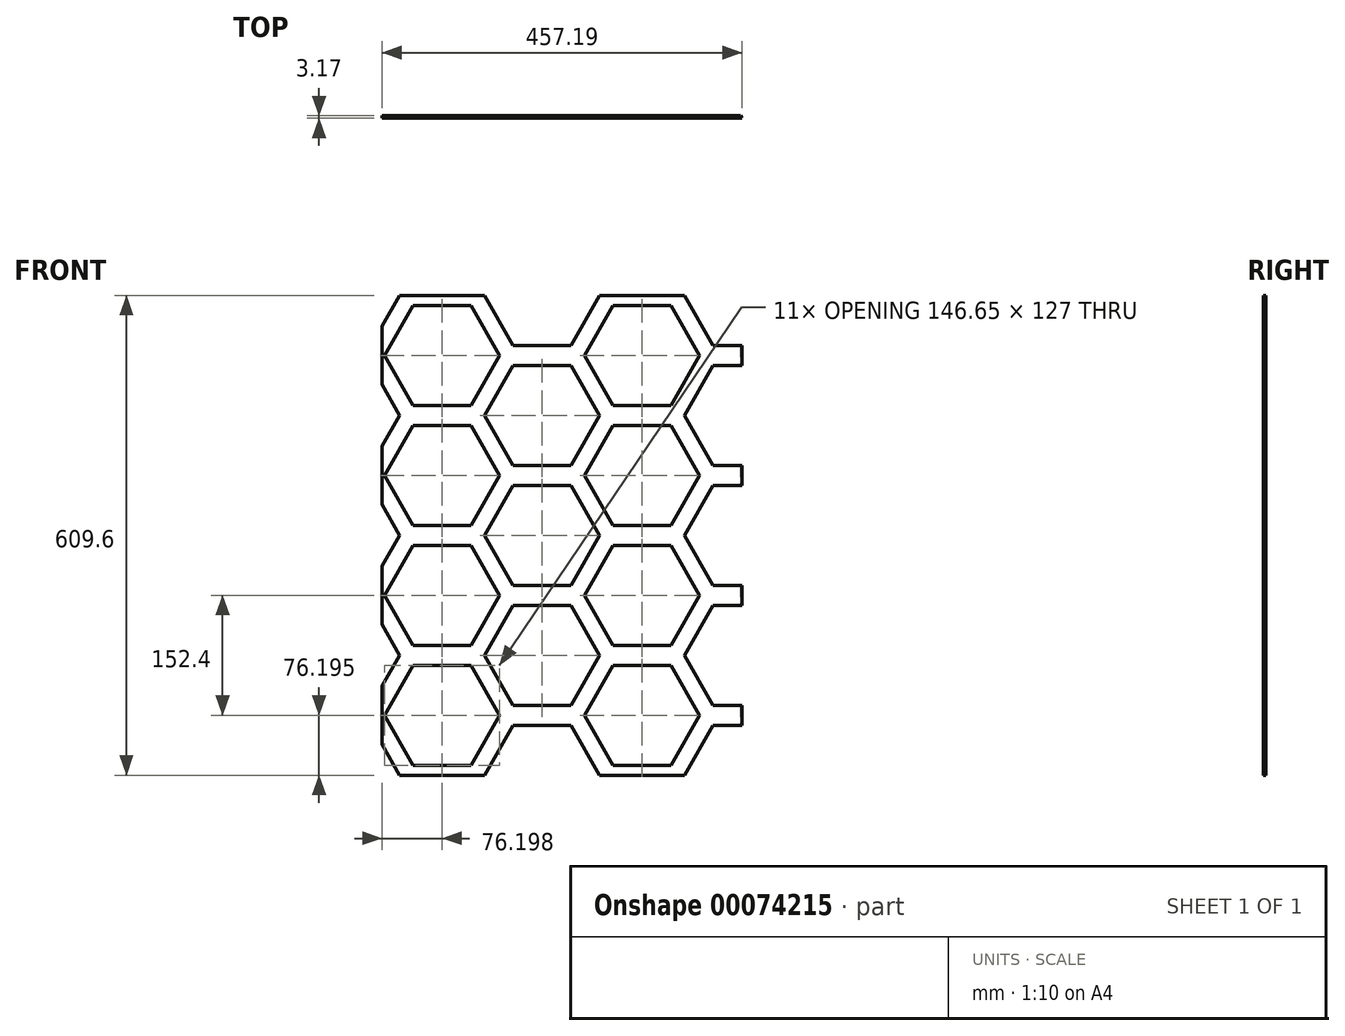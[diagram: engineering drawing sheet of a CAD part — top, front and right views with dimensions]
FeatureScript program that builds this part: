
annotation { "Feature Type Name" : "Feature", "Feature Type Description" : "" }
export const myFeature = defineFeature(function(context is Context, id is Id, definition is map)
    precondition{}
    {
        {
            var Q0;
            Q0=qCreatedBy(makeId("Front.planeOp"),FACE);
            var sketch = newSketch(context, id + "F0", { "sketchPlane" : qUnion([Q0])});
            skLineSegment(sketch, "E0.bottom", {"start": v(-264.83, 118.46) * mm, "end": v(192.37, 118.46) * mm});
            skLineSegment(sketch, "E0.top", {"start": v(-264.83, -491.14) * mm, "end": v(192.37, -491.14) * mm});
            skLineSegment(sketch, "E0.left", {"start": v(-264.83, 118.46) * mm, "end": v(-264.83, -491.14) * mm});
            skLineSegment(sketch, "E0.right", {"start": v(192.37, 118.46) * mm, "end": v(192.37, -491.14) * mm});
            skLineSegment(sketch, "E1", {"start": v(-188.63, -491.14) * mm, "end": v(-188.63, 518.04) * mm, "construction": true});
            skLineSegment(sketch, "E2", {"start": v(-264.83, -414.94) * mm, "end": v(579.47, -414.94) * mm, "construction": true});
            skCircle(sketch, "E3.cCircle", {"center": v(-188.63, -414.94) * mm, "radius": 63.5 * mm, "construction": true});
            skLineSegment(sketch, "E3.0", {"start": v(-225.3, -351.44) * mm, "end": v(-151.97, -351.44) * mm});
            skLineSegment(sketch, "E3.1", {"start": v(-151.97, -351.44) * mm, "end": v(-115.3, -414.94) * mm});
            skLineSegment(sketch, "E3.2", {"start": v(-115.3, -414.94) * mm, "end": v(-151.97, -478.44) * mm});
            skLineSegment(sketch, "E3.3", {"start": v(-151.97, -478.44) * mm, "end": v(-225.3, -478.44) * mm});
            skLineSegment(sketch, "E3.4", {"start": v(-225.3, -478.44) * mm, "end": v(-261.96, -414.94) * mm});
            skLineSegment(sketch, "E3.5", {"start": v(-261.96, -414.94) * mm, "end": v(-225.3, -351.44) * mm});
            skPoint(sketch, "E3.0.midPoint", {"position": v(-188.63, -351.44) * mm});
            skLineSegment(sketch, "E4", {"start": v(-188.63, -414.94) * mm, "end": v(-315.63, -414.94) * mm, "construction": true});
            skLineSegment(sketch, "E5", {"start": v(-315.63, -414.94) * mm, "end": v(-315.63, -491.14) * mm, "construction": true});
            skCircle(sketch, "E6.cCircle", {"center": v(-315.63, -491.14) * mm, "radius": 63.5 * mm, "construction": true});
            skLineSegment(sketch, "E6.0", {"start": v(-352.3, -427.64) * mm, "end": v(-278.97, -427.64) * mm});
            skLineSegment(sketch, "E6.1", {"start": v(-278.97, -427.64) * mm, "end": v(-242.3, -491.14) * mm});
            skLineSegment(sketch, "E6.2", {"start": v(-242.3, -491.14) * mm, "end": v(-278.97, -554.64) * mm});
            skLineSegment(sketch, "E6.3", {"start": v(-278.97, -554.64) * mm, "end": v(-352.3, -554.64) * mm});
            skLineSegment(sketch, "E6.4", {"start": v(-352.3, -554.64) * mm, "end": v(-388.96, -491.14) * mm});
            skLineSegment(sketch, "E6.5", {"start": v(-388.96, -491.14) * mm, "end": v(-352.3, -427.64) * mm});
            skPoint(sketch, "E6.0.midPoint", {"position": v(-315.63, -427.64) * mm});
            skLineSegment(sketch, "E7.0.1.0", {"start": v(-151.97, -326.04) * mm, "end": v(-225.3, -326.04) * mm});
            skLineSegment(sketch, "E7.0.1.1", {"start": v(-225.3, -199.04) * mm, "end": v(-151.97, -199.04) * mm});
            skLineSegment(sketch, "E7.0.1.2", {"start": v(-225.3, -326.04) * mm, "end": v(-261.96, -262.54) * mm});
            skLineSegment(sketch, "E7.0.1.3", {"start": v(-151.97, -199.04) * mm, "end": v(-115.3, -262.54) * mm});
            skLineSegment(sketch, "E7.0.1.4", {"start": v(-261.96, -262.54) * mm, "end": v(-225.3, -199.04) * mm});
            skLineSegment(sketch, "E7.0.1.5", {"start": v(-115.3, -262.54) * mm, "end": v(-151.97, -326.04) * mm});
            skLineSegment(sketch, "E7.0.2.0", {"start": v(-151.97, -173.64) * mm, "end": v(-225.3, -173.64) * mm});
            skLineSegment(sketch, "E7.0.2.1", {"start": v(-225.3, -46.64) * mm, "end": v(-151.97, -46.64) * mm});
            skLineSegment(sketch, "E7.0.2.2", {"start": v(-225.3, -173.64) * mm, "end": v(-261.96, -110.14) * mm});
            skLineSegment(sketch, "E7.0.2.3", {"start": v(-151.97, -46.64) * mm, "end": v(-115.3, -110.14) * mm});
            skLineSegment(sketch, "E7.0.2.4", {"start": v(-261.96, -110.14) * mm, "end": v(-225.3, -46.64) * mm});
            skLineSegment(sketch, "E7.0.2.5", {"start": v(-115.3, -110.14) * mm, "end": v(-151.97, -173.64) * mm});
            skLineSegment(sketch, "E7.0.3.0", {"start": v(-151.97, -21.24) * mm, "end": v(-225.3, -21.24) * mm});
            skLineSegment(sketch, "E7.0.3.1", {"start": v(-225.3, 105.76) * mm, "end": v(-151.97, 105.76) * mm});
            skLineSegment(sketch, "E7.0.3.2", {"start": v(-225.3, -21.24) * mm, "end": v(-261.96, 42.26) * mm});
            skLineSegment(sketch, "E7.0.3.3", {"start": v(-151.97, 105.76) * mm, "end": v(-115.3, 42.26) * mm});
            skLineSegment(sketch, "E7.0.3.4", {"start": v(-261.96, 42.26) * mm, "end": v(-225.3, 105.76) * mm});
            skLineSegment(sketch, "E7.0.3.5", {"start": v(-115.3, 42.26) * mm, "end": v(-151.97, -21.24) * mm});
            skLineSegment(sketch, "E7.1.0.0", {"start": v(102.03, -478.44) * mm, "end": v(28.7, -478.44) * mm});
            skLineSegment(sketch, "E7.1.0.1", {"start": v(28.7, -351.44) * mm, "end": v(102.03, -351.44) * mm});
            skLineSegment(sketch, "E7.1.0.2", {"start": v(28.7, -478.44) * mm, "end": v(-7.96, -414.94) * mm});
            skLineSegment(sketch, "E7.1.0.3", {"start": v(102.03, -351.44) * mm, "end": v(138.7, -414.94) * mm});
            skLineSegment(sketch, "E7.1.0.4", {"start": v(-7.96, -414.94) * mm, "end": v(28.7, -351.44) * mm});
            skLineSegment(sketch, "E7.1.0.5", {"start": v(138.7, -414.94) * mm, "end": v(102.03, -478.44) * mm});
            skLineSegment(sketch, "E7.1.1.0", {"start": v(102.03, -326.04) * mm, "end": v(28.7, -326.04) * mm});
            skLineSegment(sketch, "E7.1.1.1", {"start": v(28.7, -199.04) * mm, "end": v(102.03, -199.04) * mm});
            skLineSegment(sketch, "E7.1.1.2", {"start": v(28.7, -326.04) * mm, "end": v(-7.96, -262.54) * mm});
            skLineSegment(sketch, "E7.1.1.3", {"start": v(102.03, -199.04) * mm, "end": v(138.7, -262.54) * mm});
            skLineSegment(sketch, "E7.1.1.4", {"start": v(-7.96, -262.54) * mm, "end": v(28.7, -199.04) * mm});
            skLineSegment(sketch, "E7.1.1.5", {"start": v(138.7, -262.54) * mm, "end": v(102.03, -326.04) * mm});
            skLineSegment(sketch, "E7.1.2.0", {"start": v(102.03, -173.64) * mm, "end": v(28.7, -173.64) * mm});
            skLineSegment(sketch, "E7.1.2.1", {"start": v(28.7, -46.64) * mm, "end": v(102.03, -46.64) * mm});
            skLineSegment(sketch, "E7.1.2.2", {"start": v(28.7, -173.64) * mm, "end": v(-7.96, -110.14) * mm});
            skLineSegment(sketch, "E7.1.2.3", {"start": v(102.03, -46.64) * mm, "end": v(138.7, -110.14) * mm});
            skLineSegment(sketch, "E7.1.2.4", {"start": v(-7.96, -110.14) * mm, "end": v(28.7, -46.64) * mm});
            skLineSegment(sketch, "E7.1.2.5", {"start": v(138.7, -110.14) * mm, "end": v(102.03, -173.64) * mm});
            skLineSegment(sketch, "E7.1.3.0", {"start": v(102.03, -21.24) * mm, "end": v(28.7, -21.24) * mm});
            skLineSegment(sketch, "E7.1.3.1", {"start": v(28.7, 105.76) * mm, "end": v(102.03, 105.76) * mm});
            skLineSegment(sketch, "E7.1.3.2", {"start": v(28.7, -21.24) * mm, "end": v(-7.96, 42.26) * mm});
            skLineSegment(sketch, "E7.1.3.3", {"start": v(102.03, 105.76) * mm, "end": v(138.7, 42.26) * mm});
            skLineSegment(sketch, "E7.1.3.4", {"start": v(-7.96, 42.26) * mm, "end": v(28.7, 105.76) * mm});
            skLineSegment(sketch, "E7.1.3.5", {"start": v(138.7, 42.26) * mm, "end": v(102.03, -21.24) * mm});
            skLineSegment(sketch, "E7.direction1", {"start": v(-261.96, -414.94) * mm, "end": v(-7.96, -414.94) * mm, "construction": true});
            skLineSegment(sketch, "E7.direction2", {"start": v(-261.96, -414.94) * mm, "end": v(-261.96, -262.54) * mm, "construction": true});
            skLineSegment(sketch, "E8.0.1.0", {"start": v(-278.97, -402.24) * mm, "end": v(-352.3, -402.24) * mm});
            skLineSegment(sketch, "E8.0.1.1", {"start": v(-352.3, -275.24) * mm, "end": v(-278.97, -275.24) * mm});
            skLineSegment(sketch, "E8.0.1.2", {"start": v(-352.3, -402.24) * mm, "end": v(-388.96, -338.74) * mm});
            skLineSegment(sketch, "E8.0.1.3", {"start": v(-278.97, -275.24) * mm, "end": v(-242.3, -338.74) * mm});
            skLineSegment(sketch, "E8.0.1.4", {"start": v(-388.96, -338.74) * mm, "end": v(-352.3, -275.24) * mm});
            skLineSegment(sketch, "E8.0.1.5", {"start": v(-242.3, -338.74) * mm, "end": v(-278.97, -402.24) * mm});
            skLineSegment(sketch, "E8.0.2.0", {"start": v(-278.97, -249.84) * mm, "end": v(-352.3, -249.84) * mm});
            skLineSegment(sketch, "E8.0.2.1", {"start": v(-352.3, -122.84) * mm, "end": v(-278.97, -122.84) * mm});
            skLineSegment(sketch, "E8.0.2.2", {"start": v(-352.3, -249.84) * mm, "end": v(-388.96, -186.34) * mm});
            skLineSegment(sketch, "E8.0.2.3", {"start": v(-278.97, -122.84) * mm, "end": v(-242.3, -186.34) * mm});
            skLineSegment(sketch, "E8.0.2.4", {"start": v(-388.96, -186.34) * mm, "end": v(-352.3, -122.84) * mm});
            skLineSegment(sketch, "E8.0.2.5", {"start": v(-242.3, -186.34) * mm, "end": v(-278.97, -249.84) * mm});
            skLineSegment(sketch, "E8.0.3.0", {"start": v(-278.97, -97.44) * mm, "end": v(-352.3, -97.44) * mm});
            skLineSegment(sketch, "E8.0.3.1", {"start": v(-352.3, 29.56) * mm, "end": v(-278.97, 29.56) * mm});
            skLineSegment(sketch, "E8.0.3.2", {"start": v(-352.3, -97.44) * mm, "end": v(-388.96, -33.94) * mm});
            skLineSegment(sketch, "E8.0.3.3", {"start": v(-278.97, 29.56) * mm, "end": v(-242.3, -33.94) * mm});
            skLineSegment(sketch, "E8.0.3.4", {"start": v(-388.96, -33.94) * mm, "end": v(-352.3, 29.56) * mm});
            skLineSegment(sketch, "E8.0.3.5", {"start": v(-242.3, -33.94) * mm, "end": v(-278.97, -97.44) * mm});
            skLineSegment(sketch, "E8.0.4.0", {"start": v(-278.97, 54.96) * mm, "end": v(-352.3, 54.96) * mm});
            skLineSegment(sketch, "E8.0.4.1", {"start": v(-352.3, 181.96) * mm, "end": v(-278.97, 181.96) * mm});
            skLineSegment(sketch, "E8.0.4.2", {"start": v(-352.3, 54.96) * mm, "end": v(-388.96, 118.46) * mm});
            skLineSegment(sketch, "E8.0.4.3", {"start": v(-278.97, 181.96) * mm, "end": v(-242.3, 118.46) * mm});
            skLineSegment(sketch, "E8.0.4.4", {"start": v(-388.96, 118.46) * mm, "end": v(-352.3, 181.96) * mm});
            skLineSegment(sketch, "E8.0.4.5", {"start": v(-242.3, 118.46) * mm, "end": v(-278.97, 54.96) * mm});
            skLineSegment(sketch, "E8.1.0.0", {"start": v(-24.97, -554.64) * mm, "end": v(-98.3, -554.64) * mm});
            skLineSegment(sketch, "E8.1.0.1", {"start": v(-98.3, -427.64) * mm, "end": v(-24.97, -427.64) * mm});
            skLineSegment(sketch, "E8.1.0.2", {"start": v(-98.3, -554.64) * mm, "end": v(-134.96, -491.14) * mm});
            skLineSegment(sketch, "E8.1.0.3", {"start": v(-24.97, -427.64) * mm, "end": v(11.7, -491.14) * mm});
            skLineSegment(sketch, "E8.1.0.4", {"start": v(-134.96, -491.14) * mm, "end": v(-98.3, -427.64) * mm});
            skLineSegment(sketch, "E8.1.0.5", {"start": v(11.7, -491.14) * mm, "end": v(-24.97, -554.64) * mm});
            skLineSegment(sketch, "E8.1.1.0", {"start": v(-24.97, -402.24) * mm, "end": v(-98.3, -402.24) * mm});
            skLineSegment(sketch, "E8.1.1.1", {"start": v(-98.3, -275.24) * mm, "end": v(-24.97, -275.24) * mm});
            skLineSegment(sketch, "E8.1.1.2", {"start": v(-98.3, -402.24) * mm, "end": v(-134.96, -338.74) * mm});
            skLineSegment(sketch, "E8.1.1.3", {"start": v(-24.97, -275.24) * mm, "end": v(11.7, -338.74) * mm});
            skLineSegment(sketch, "E8.1.1.4", {"start": v(-134.96, -338.74) * mm, "end": v(-98.3, -275.24) * mm});
            skLineSegment(sketch, "E8.1.1.5", {"start": v(11.7, -338.74) * mm, "end": v(-24.97, -402.24) * mm});
            skLineSegment(sketch, "E8.1.2.0", {"start": v(-24.97, -249.84) * mm, "end": v(-98.3, -249.84) * mm});
            skLineSegment(sketch, "E8.1.2.1", {"start": v(-98.3, -122.84) * mm, "end": v(-24.97, -122.84) * mm});
            skLineSegment(sketch, "E8.1.2.2", {"start": v(-98.3, -249.84) * mm, "end": v(-134.96, -186.34) * mm});
            skLineSegment(sketch, "E8.1.2.3", {"start": v(-24.97, -122.84) * mm, "end": v(11.7, -186.34) * mm});
            skLineSegment(sketch, "E8.1.2.4", {"start": v(-134.96, -186.34) * mm, "end": v(-98.3, -122.84) * mm});
            skLineSegment(sketch, "E8.1.2.5", {"start": v(11.7, -186.34) * mm, "end": v(-24.97, -249.84) * mm});
            skLineSegment(sketch, "E8.1.3.0", {"start": v(-24.97, -97.44) * mm, "end": v(-98.3, -97.44) * mm});
            skLineSegment(sketch, "E8.1.3.1", {"start": v(-98.3, 29.56) * mm, "end": v(-24.97, 29.56) * mm});
            skLineSegment(sketch, "E8.1.3.2", {"start": v(-98.3, -97.44) * mm, "end": v(-134.96, -33.94) * mm});
            skLineSegment(sketch, "E8.1.3.3", {"start": v(-24.97, 29.56) * mm, "end": v(11.7, -33.94) * mm});
            skLineSegment(sketch, "E8.1.3.4", {"start": v(-134.96, -33.94) * mm, "end": v(-98.3, 29.56) * mm});
            skLineSegment(sketch, "E8.1.3.5", {"start": v(11.7, -33.94) * mm, "end": v(-24.97, -97.44) * mm});
            skLineSegment(sketch, "E8.1.4.0", {"start": v(-24.97, 54.96) * mm, "end": v(-98.3, 54.96) * mm});
            skLineSegment(sketch, "E8.1.4.1", {"start": v(-98.3, 181.96) * mm, "end": v(-24.97, 181.96) * mm});
            skLineSegment(sketch, "E8.1.4.2", {"start": v(-98.3, 54.96) * mm, "end": v(-134.96, 118.46) * mm});
            skLineSegment(sketch, "E8.1.4.3", {"start": v(-24.97, 181.96) * mm, "end": v(11.7, 118.46) * mm});
            skLineSegment(sketch, "E8.1.4.4", {"start": v(-134.96, 118.46) * mm, "end": v(-98.3, 181.96) * mm});
            skLineSegment(sketch, "E8.1.4.5", {"start": v(11.7, 118.46) * mm, "end": v(-24.97, 54.96) * mm});
            skLineSegment(sketch, "E8.2.0.0", {"start": v(229.03, -554.64) * mm, "end": v(155.7, -554.64) * mm});
            skLineSegment(sketch, "E8.2.0.1", {"start": v(155.7, -427.64) * mm, "end": v(229.03, -427.64) * mm});
            skLineSegment(sketch, "E8.2.0.2", {"start": v(155.7, -554.64) * mm, "end": v(119.04, -491.14) * mm});
            skLineSegment(sketch, "E8.2.0.3", {"start": v(229.03, -427.64) * mm, "end": v(265.7, -491.14) * mm});
            skLineSegment(sketch, "E8.2.0.4", {"start": v(119.04, -491.14) * mm, "end": v(155.7, -427.64) * mm});
            skLineSegment(sketch, "E8.2.0.5", {"start": v(265.7, -491.14) * mm, "end": v(229.03, -554.64) * mm});
            skLineSegment(sketch, "E8.2.1.0", {"start": v(229.03, -402.24) * mm, "end": v(155.7, -402.24) * mm});
            skLineSegment(sketch, "E8.2.1.1", {"start": v(155.7, -275.24) * mm, "end": v(229.03, -275.24) * mm});
            skLineSegment(sketch, "E8.2.1.2", {"start": v(155.7, -402.24) * mm, "end": v(119.04, -338.74) * mm});
            skLineSegment(sketch, "E8.2.1.3", {"start": v(229.03, -275.24) * mm, "end": v(265.7, -338.74) * mm});
            skLineSegment(sketch, "E8.2.1.4", {"start": v(119.04, -338.74) * mm, "end": v(155.7, -275.24) * mm});
            skLineSegment(sketch, "E8.2.1.5", {"start": v(265.7, -338.74) * mm, "end": v(229.03, -402.24) * mm});
            skLineSegment(sketch, "E8.2.2.0", {"start": v(229.03, -249.84) * mm, "end": v(155.7, -249.84) * mm});
            skLineSegment(sketch, "E8.2.2.1", {"start": v(155.7, -122.84) * mm, "end": v(229.03, -122.84) * mm});
            skLineSegment(sketch, "E8.2.2.2", {"start": v(155.7, -249.84) * mm, "end": v(119.04, -186.34) * mm});
            skLineSegment(sketch, "E8.2.2.3", {"start": v(229.03, -122.84) * mm, "end": v(265.7, -186.34) * mm});
            skLineSegment(sketch, "E8.2.2.4", {"start": v(119.04, -186.34) * mm, "end": v(155.7, -122.84) * mm});
            skLineSegment(sketch, "E8.2.2.5", {"start": v(265.7, -186.34) * mm, "end": v(229.03, -249.84) * mm});
            skLineSegment(sketch, "E8.2.3.0", {"start": v(229.03, -97.44) * mm, "end": v(155.7, -97.44) * mm});
            skLineSegment(sketch, "E8.2.3.1", {"start": v(155.7, 29.56) * mm, "end": v(229.03, 29.56) * mm});
            skLineSegment(sketch, "E8.2.3.2", {"start": v(155.7, -97.44) * mm, "end": v(119.04, -33.94) * mm});
            skLineSegment(sketch, "E8.2.3.3", {"start": v(229.03, 29.56) * mm, "end": v(265.7, -33.94) * mm});
            skLineSegment(sketch, "E8.2.3.4", {"start": v(119.04, -33.94) * mm, "end": v(155.7, 29.56) * mm});
            skLineSegment(sketch, "E8.2.3.5", {"start": v(265.7, -33.94) * mm, "end": v(229.03, -97.44) * mm});
            skLineSegment(sketch, "E8.2.4.0", {"start": v(229.03, 54.96) * mm, "end": v(155.7, 54.96) * mm});
            skLineSegment(sketch, "E8.2.4.1", {"start": v(155.7, 181.96) * mm, "end": v(229.03, 181.96) * mm});
            skLineSegment(sketch, "E8.2.4.2", {"start": v(155.7, 54.96) * mm, "end": v(119.04, 118.46) * mm});
            skLineSegment(sketch, "E8.2.4.3", {"start": v(229.03, 181.96) * mm, "end": v(265.7, 118.46) * mm});
            skLineSegment(sketch, "E8.2.4.4", {"start": v(119.04, 118.46) * mm, "end": v(155.7, 181.96) * mm});
            skLineSegment(sketch, "E8.2.4.5", {"start": v(265.7, 118.46) * mm, "end": v(229.03, 54.96) * mm});
            skLineSegment(sketch, "E8.direction1", {"start": v(-388.96, -491.14) * mm, "end": v(-134.96, -491.14) * mm, "construction": true});
            skLineSegment(sketch, "E8.direction2", {"start": v(-388.96, -491.14) * mm, "end": v(-388.96, -338.74) * mm, "construction": true});
            skSolve(sketch);
        }
        {
            var Q0;
            Q0=makeQuery(id+"F0.imprint","IMPRINT",FACE,{"disambiguationData":[TD([[makeQuery(id+"F0.imprint","IMPRINT",EDGE,{"derivedFrom":sQuery(id+"F0.wireOp",EDGE,"E3.0")}),1.0]])]});
            extrude(context, id + "F1", {"entities" : qUnion([Q0]), "depth" : 3.17 * mm});
        }
        {
            var Q0;
            {var subQ0=sQuery(id+"F0.wireOp",EDGE,"E0.right");Q0=makeQuery(id+"F1.opExtrude","CAP_EDGE",EDGE,{"disambiguationData":[OSD([subQ0]),TDD([makeQuery(id+"F0.imprint","IMPRINT",EDGE,{"disambiguationData":[TD([[makeQuery(id+"F0.imprint","INTERSECT",VERTEX,{"derivedFrom":[subQ0,sQuery(id+"F0.wireOp",EDGE,"E8.2.4.0")]}),-1.0]])],"derivedFrom":subQ0})])],"isStart":true});}
            chamfer(context, id + "F2", {"entities" : qUnion([Q0]), "chamferType" : ChamferType.OFFSET_ANGLE, "width" : 1.84 * mm, "oppositeDirection" : false, "angle" : 60 * degree, "tangentPropagation" : true});
        }
        {
            var Q0;
            {var subQ0=sQuery(id+"F0.wireOp",EDGE,"E0.right");Q0=makeQuery(id+"F1.opExtrude","CAP_EDGE",EDGE,{"disambiguationData":[OSD([subQ0]),TDD([makeQuery(id+"F0.imprint","IMPRINT",EDGE,{"disambiguationData":[TD([[makeQuery(id+"F0.imprint","INTERSECT",VERTEX,{"derivedFrom":[subQ0,sQuery(id+"F0.wireOp",EDGE,"E8.2.3.0")]}),-1.0]])],"derivedFrom":subQ0})])],"isStart":true});}
            chamfer(context, id + "F3", {"entities" : qUnion([Q0]), "chamferType" : ChamferType.OFFSET_ANGLE, "width" : 1.91 * mm, "oppositeDirection" : false, "angle" : 60 * degree, "tangentPropagation" : true});
        }
        {
            var Q0;
            {var subQ0=sQuery(id+"F0.wireOp",EDGE,"E0.right");Q0=makeQuery(id+"F1.opExtrude","CAP_EDGE",EDGE,{"disambiguationData":[OSD([subQ0]),TDD([makeQuery(id+"F0.imprint","IMPRINT",EDGE,{"disambiguationData":[TD([[makeQuery(id+"F0.imprint","INTERSECT",VERTEX,{"derivedFrom":[subQ0,sQuery(id+"F0.wireOp",EDGE,"E8.2.2.0")]}),-1.0]])],"derivedFrom":subQ0})])],"isStart":true});}
            chamfer(context, id + "F4", {"entities" : qUnion([Q0]), "chamferType" : ChamferType.OFFSET_ANGLE, "width" : 1.84 * mm, "oppositeDirection" : false, "angle" : 60 * degree, "tangentPropagation" : true});
        }
        {
            var Q0;
            {var subQ0=sQuery(id+"F0.wireOp",EDGE,"E0.right");Q0=makeQuery(id+"F1.opExtrude","CAP_EDGE",EDGE,{"disambiguationData":[OSD([subQ0]),TDD([makeQuery(id+"F0.imprint","IMPRINT",EDGE,{"disambiguationData":[TD([[makeQuery(id+"F0.imprint","INTERSECT",VERTEX,{"derivedFrom":[subQ0,sQuery(id+"F0.wireOp",EDGE,"E8.2.1.0")]}),-1.0]])],"derivedFrom":subQ0})])],"isStart":true});}
            chamfer(context, id + "F5", {"entities" : qUnion([Q0]), "chamferType" : ChamferType.OFFSET_ANGLE, "width" : 1.84 * mm, "oppositeDirection" : false, "angle" : 60 * degree, "tangentPropagation" : true});
        }
    });
